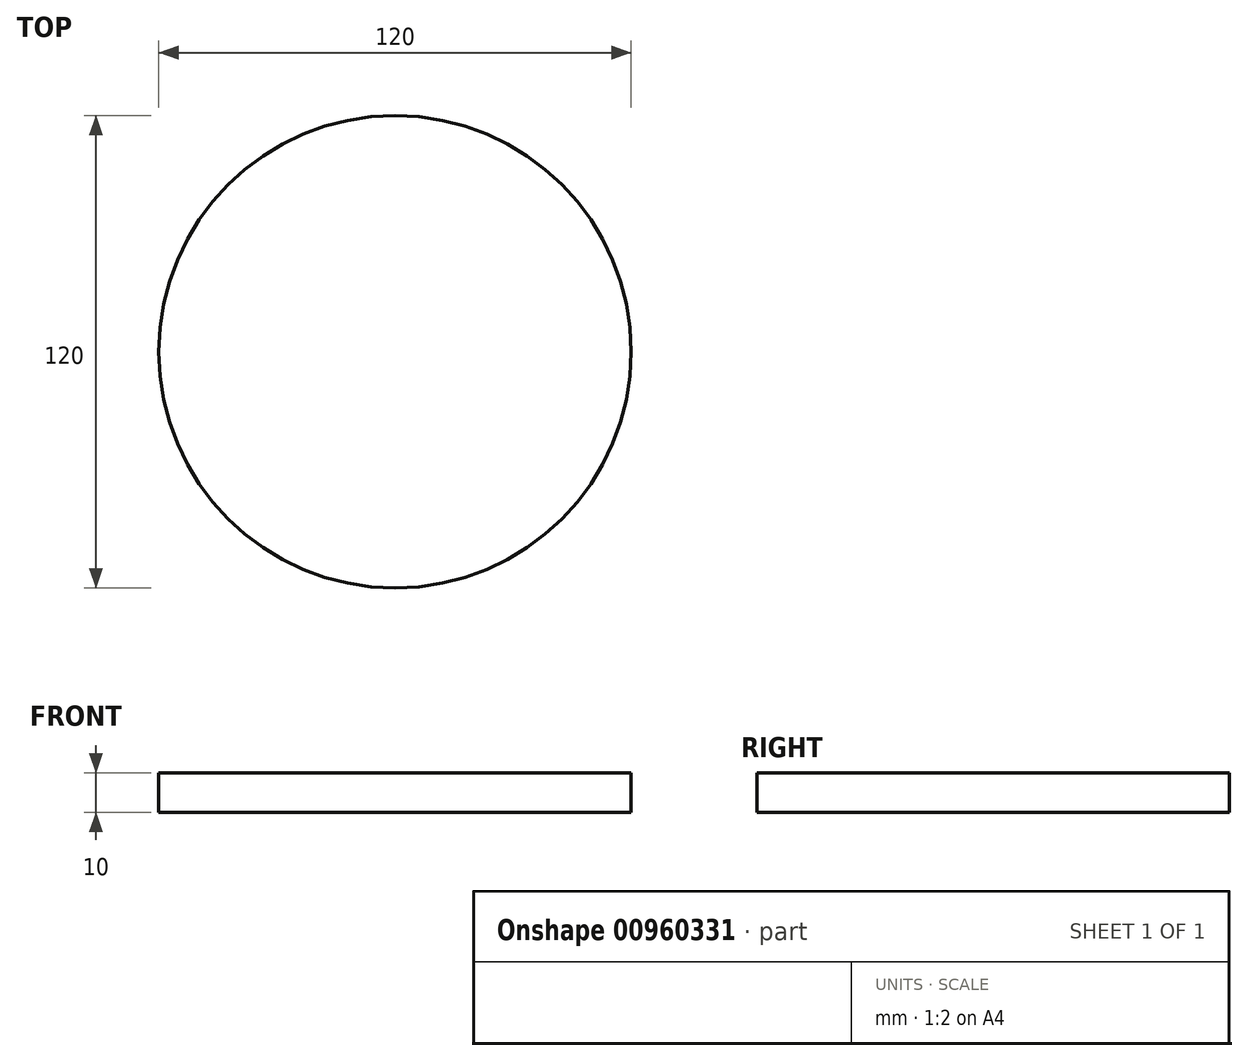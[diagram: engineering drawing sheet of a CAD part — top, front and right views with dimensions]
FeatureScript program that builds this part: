
annotation { "Feature Type Name" : "Feature", "Feature Type Description" : "" }
export const myFeature = defineFeature(function(context is Context, id is Id, definition is map)
    precondition{}
    {
        {
            var Q0;
            Q0=qCreatedBy(makeId("Top.planeOp"),FACE);
            var sketch = newSketch(context, id + "F0", { "sketchPlane" : qUnion([Q0])});
            skCircle(sketch, "E0", {"center": v(0, 0) * mm, "radius": 60 * mm});
            skSolve(sketch);
        }
        {
            var Q0;
            Q0=makeQuery(id+"F0.imprint","IMPRINT",FACE,{"disambiguationData":[TD([[makeQuery(id+"F0.imprint","IMPRINT",EDGE,{"derivedFrom":sQuery(id+"F0.wireOp",EDGE,"E0")}),1.0]])]});
            extrude(context, id + "F1", {"entities" : qUnion([Q0]), "depth" : 10 * mm, "offsetDistance" : 25 * mm});
        }
    });
